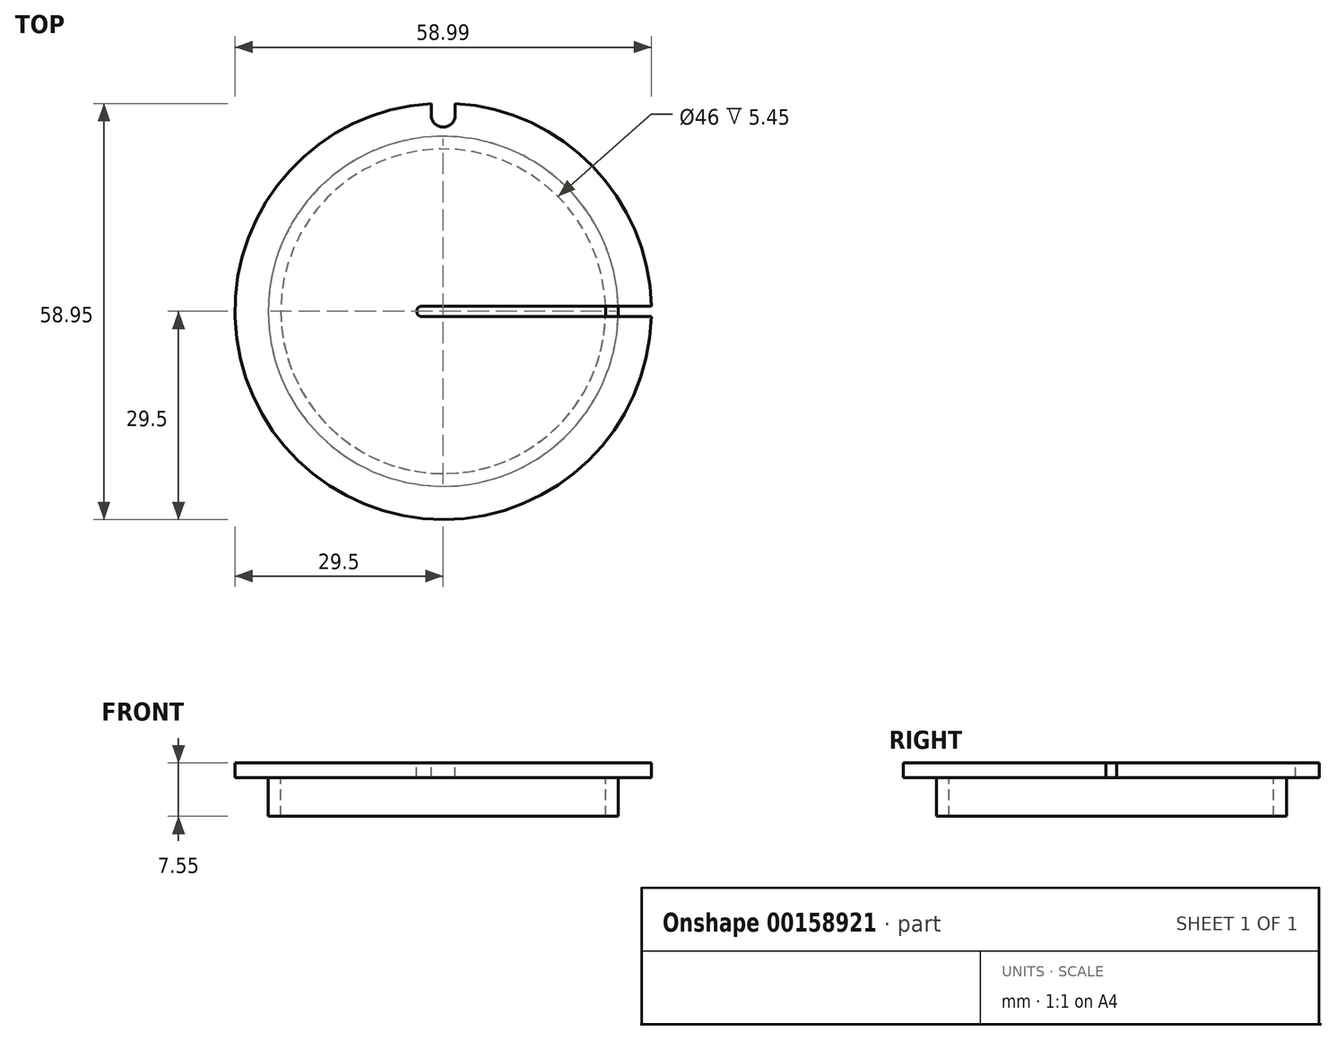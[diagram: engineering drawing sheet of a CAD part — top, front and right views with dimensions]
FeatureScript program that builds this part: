
annotation { "Feature Type Name" : "Feature", "Feature Type Description" : "" }
export const myFeature = defineFeature(function(context is Context, id is Id, definition is map)
    precondition{}
    {
        {
            var Q0;
            Q0=qCreatedBy(makeId("Top.planeOp"),FACE);
            var sketch = newSketch(context, id + "F0", { "sketchPlane" : qUnion([Q0])});
            skCircle(sketch, "E0", {"center": v(0, 0) * mm, "radius": 29.5 * mm});
            skSolve(sketch);
        }
        {
            var Q0;
            Q0=qCreatedBy(makeId("Front.planeOp"),FACE);
            var sketch = newSketch(context, id + "F1", { "sketchPlane" : qUnion([Q0])});
            skLineSegment(sketch, "E1", {"start": v(0, 0) * mm, "end": v(0, 10) * mm, "construction": true});
            skSolve(sketch);
        }
        {
            var Q0;
            Q0 = qSketchRegion(id + "F0", true);
            extrude(context, id + "F2", {"entities" : qUnion([Q0]), "depth" : 2.1 * mm});
        }
        {
            var Q0;
            Q0=makeQuery(id+"F2.opExtrude","CAP_FACE",FACE,{"disambiguationData":[OSD([sQuery(id+"F0.wireOp",EDGE,"E0")])],"isStart":false});
            var sketch = newSketch(context, id + "F3", { "sketchPlane" : qUnion([Q0])});
            skLineSegment(sketch, "E2", {"start": v(0, 0) * mm, "end": v(0, 29.5) * mm, "construction": true});
            skLineSegment(sketch, "E3.0", {"start": v(1.7, 27.8) * mm, "end": v(1.7, 29.45) * mm});
            skLineSegment(sketch, "E4.MirrorCS", {"start": v(-1.7, 27.8) * mm, "end": v(-1.7, 29.45) * mm});
            skArc(sketch, "E5", {"start": v(-1.7, 27.8) * mm, "mid": v(0, 26.1) * mm, "end": v(1.7, 27.8) * mm});
            skPoint(sketch, "E6.orphan", {"position": v(1.7, 0) * mm});
            skPoint(sketch, "E7.orphan", {"position": v(-1.7, 0) * mm});
            skArc(sketch, "E8", {"start": v(1.7, 29.45) * mm, "mid": v(0, 29.5) * mm, "end": v(-1.7, 29.45) * mm});
            skSolve(sketch);
        }
        {
            var Q0;
            Q0=makeQuery(id+"F3.imprint","IMPRINT",FACE,{"disambiguationData":[TD([[makeQuery(id+"F3.imprint","IMPRINT",EDGE,{"derivedFrom":sQuery(id+"F3.wireOp",EDGE,"E3.0")}),1.0]])]});
            extrude(context, id + "F4", {"entities" : qUnion([Q0]), "operationType" : NewBodyOperationType.REMOVE, "endBound" : BoundingType.UP_TO_NEXT, "oppositeDirection" : true, "depth" : 25 * mm});
        }
        {
            var Q0;
            Q0=makeQuery(id+"F2.opExtrude","CAP_FACE",FACE,{"disambiguationData":[OSD([sQuery(id+"F0.wireOp",EDGE,"E0")])],"isStart":false});
            var sketch = newSketch(context, id + "F5", { "sketchPlane" : qUnion([Q0])});
            skLineSegment(sketch, "E9", {"start": v(-3, 0) * mm, "end": v(29.5, 0) * mm, "construction": true});
            skLineSegment(sketch, "E10", {"start": v(-3, -0.75) * mm, "end": v(29.5, -0.75) * mm});
            skLineSegment(sketch, "E11.MirrorCS", {"start": v(-3, 0.75) * mm, "end": v(29.5, 0.75) * mm});
            skArc(sketch, "E12", {"start": v(-3, 0.75) * mm, "mid": v(-3.75, 0) * mm, "end": v(-3, -0.75) * mm});
            skSolve(sketch);
        }
        {
            var Q0;
            {var subQ0=sQuery(id+"F5.wireOp",EDGE,"E10");Q0=makeQuery(id+"F5.imprint","IMPRINT",FACE,{"disambiguationData":[TD([[makeQuery(id+"F5.imprint","IMPRINT",EDGE,{"derivedFrom":subQ0}),1.0]])]});}
            extrude(context, id + "F6", {"entities" : qUnion([Q0]), "operationType" : NewBodyOperationType.REMOVE, "endBound" : BoundingType.UP_TO_NEXT, "oppositeDirection" : true, "depth" : 25 * mm});
        }
        {
            var Q0;
            Q0=makeQuery(id+"F2.opExtrude","CAP_FACE",FACE,{"disambiguationData":[OSD([sQuery(id+"F0.wireOp",EDGE,"E0")])],"isStart":true});
            var sketch = newSketch(context, id + "F7", { "sketchPlane" : qUnion([Q0])});
            skCircle(sketch, "E13", {"center": v(0, 0) * mm, "radius": 24.8 * mm});
            skCircle(sketch, "E14", {"center": v(0, 0) * mm, "radius": 23 * mm});
            skSolve(sketch);
        }
        {
            var Q0;
            {var subQ0=sQuery(id+"F7.wireOp",EDGE,"E13");var subQ1=makeQuery(id+"F6.boolean.opBoolean","COPY",EDGE,{"derivedFrom":makeQuery(id+"F6.opExtrude","CAP_EDGE",EDGE,{"disambiguationData":[OSD([sQuery(id+"F5.wireOp",EDGE,"E10")])],"isStart":false})});var subQ2=makeQuery(id+"F7.imprint","INTERSECT",VERTEX,{"derivedFrom":[subQ1,subQ0]});Q0=makeQuery(id+"F7.imprint","IMPRINT",FACE,{"disambiguationData":[TD([[makeQuery(id+"F7.imprint","IMPRINT",EDGE,{"disambiguationData":[TD([[subQ2,-1.0]])],"derivedFrom":subQ0}),1.0]])]});}
            extrude(context, id + "F8", {"entities" : qUnion([Q0]), "operationType" : NewBodyOperationType.ADD, "depth" : 5.45 * mm});
        }
    });
